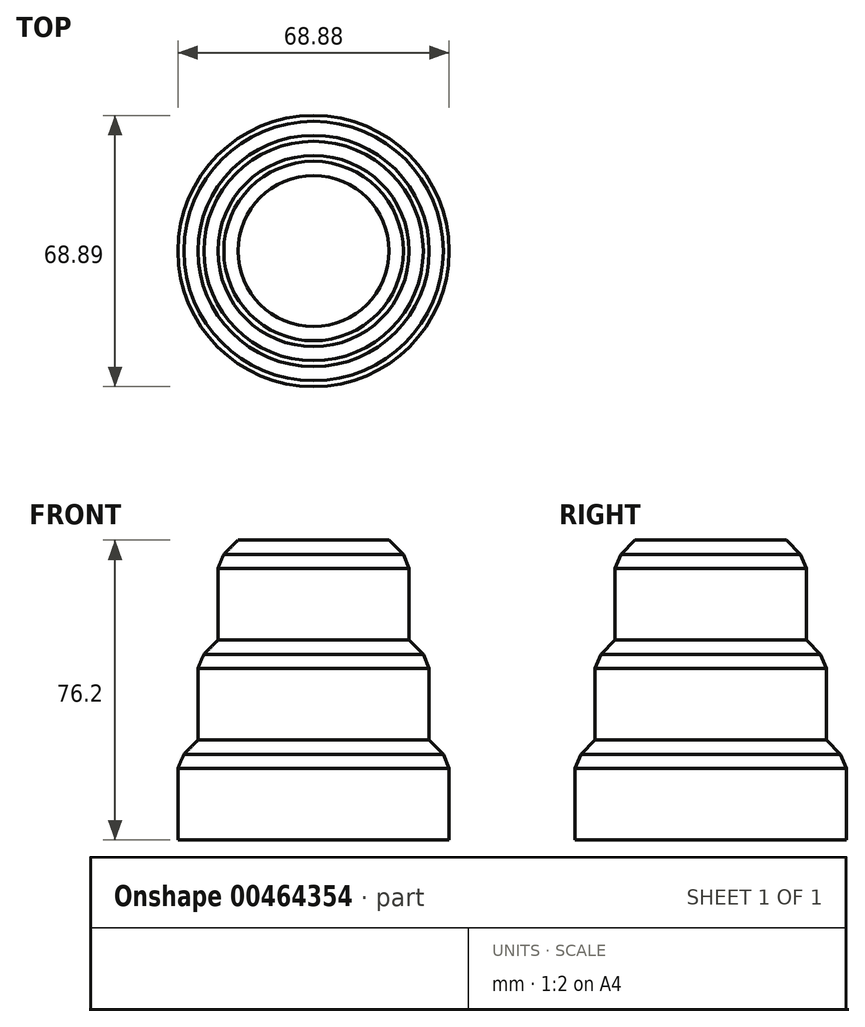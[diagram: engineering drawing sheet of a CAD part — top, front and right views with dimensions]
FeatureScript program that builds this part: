
annotation { "Feature Type Name" : "Feature", "Feature Type Description" : "" }
export const myFeature = defineFeature(function(context is Context, id is Id, definition is map)
    precondition{}
    {
        {
            var Q0;
            Q0=qCreatedBy(makeId("Top.planeOp"),FACE);
            var sketch = newSketch(context, id + "F0", { "sketchPlane" : qUnion([Q0])});
            skCircle(sketch, "E0", {"center": v(-39.93, 17.53) * mm, "radius": 34.44 * mm});
            skSolve(sketch);
        }
        {
            var Q0;
            Q0=makeQuery(id+"F0.imprint","IMPRINT",FACE,{"disambiguationData":[TD([[makeQuery(id+"F0.imprint","IMPRINT",EDGE,{"derivedFrom":sQuery(id+"F0.wireOp",EDGE,"E0")}),1.0]])]});
            extrude(context, id + "F1", {"entities" : qUnion([Q0]), "depth" : 25.4 * mm});
        }
        {
            var Q0;
            Q0=makeQuery(id+"F1.opExtrude","CAP_EDGE",EDGE,{"disambiguationData":[OSD([sQuery(id+"F0.wireOp",EDGE,"E0")])],"isStart":false});
            chamfer(context, id + "F2", {"entities" : qUnion([Q0]), "width" : 5.08 * mm, "tangentPropagation" : true});
        }
        {
            var Q0;
            {var subQ0=sQuery(id+"F0.wireOp",EDGE,"E0");Q0=makeQuery(id+"F2.opChamfer","BLEND_EDGE",EDGE,{"blendedFrom":[makeQuery(id+"F1.opExtrude","CAP_EDGE",EDGE,{"disambiguationData":[OSD([subQ0])],"isStart":false}),makeQuery(id+"F1.opExtrude","SWEPT_FACE",FACE,{"disambiguationData":[OSD([subQ0])]})],"blendedInto":[makeQuery(id+"F1.opExtrude","SWEPT_FACE",FACE,{"disambiguationData":[OSD([subQ0])]})]});}
            chamfer(context, id + "F3", {"entities" : qUnion([Q0]), "width" : 5.08 * mm, "tangentPropagation" : true});
        }
        {
            var Q0;
            Q0=makeQuery(id+"F1.opExtrude","CAP_FACE",FACE,{"disambiguationData":[OSD([sQuery(id+"F0.wireOp",EDGE,"E0")])],"isStart":false});
            extrude(context, id + "F4", {"entities" : qUnion([Q0]), "operationType" : NewBodyOperationType.ADD, "depth" : 25.4 * mm});
        }
        {
            var Q0;
            Q0=makeQuery(id+"F4.opExtrude","CAP_EDGE",EDGE,{"disambiguationData":[OSD([sQuery(id+"F0.wireOp",EDGE,"E0")])],"isStart":false});
            chamfer(context, id + "F5", {"entities" : qUnion([Q0]), "width" : 5.08 * mm, "tangentPropagation" : true});
        }
        {
            var Q0;
            Q0=makeQuery(id+"F4.opExtrude","CAP_FACE",FACE,{"disambiguationData":[OSD([sQuery(id+"F0.wireOp",EDGE,"E0")])],"isStart":false});
            extrude(context, id + "F6", {"entities" : qUnion([Q0]), "operationType" : NewBodyOperationType.ADD, "depth" : 25.4 * mm});
        }
        {
            var Q0;
            Q0=makeQuery(id+"F6.opExtrude","CAP_EDGE",EDGE,{"disambiguationData":[OSD([sQuery(id+"F0.wireOp",EDGE,"E0")])],"isStart":false});
            chamfer(context, id + "F7", {"entities" : qUnion([Q0]), "width" : 5.08 * mm, "tangentPropagation" : true});
        }
        {
            var Q0;
            {var subQ0=sQuery(id+"F0.wireOp",EDGE,"E0");Q0=makeQuery(id+"F7.opChamfer","BLEND_EDGE",EDGE,{"blendedFrom":[makeQuery(id+"F6.opExtrude","CAP_EDGE",EDGE,{"disambiguationData":[OSD([subQ0])],"isStart":false}),makeQuery(id+"F6.opExtrude","SWEPT_FACE",FACE,{"disambiguationData":[OSD([subQ0])]})],"blendedInto":[makeQuery(id+"F6.opExtrude","SWEPT_FACE",FACE,{"disambiguationData":[OSD([subQ0])]})]});}
            chamfer(context, id + "F8", {"entities" : qUnion([Q0]), "width" : 5.08 * mm, "tangentPropagation" : true});
        }
        {
            var Q0;
            {var subQ0=sQuery(id+"F0.wireOp",EDGE,"E0");Q0=makeQuery(id+"F5.opChamfer","BLEND_EDGE",EDGE,{"blendedFrom":[makeQuery(id+"F4.opExtrude","CAP_EDGE",EDGE,{"disambiguationData":[OSD([subQ0])],"isStart":false}),makeQuery(id+"F4.opExtrude","SWEPT_FACE",FACE,{"disambiguationData":[OSD([subQ0])]})],"blendedInto":[makeQuery(id+"F4.opExtrude","SWEPT_FACE",FACE,{"disambiguationData":[OSD([subQ0])]})]});}
            chamfer(context, id + "F9", {"entities" : qUnion([Q0]), "width" : 5.08 * mm, "tangentPropagation" : true});
        }
    });
